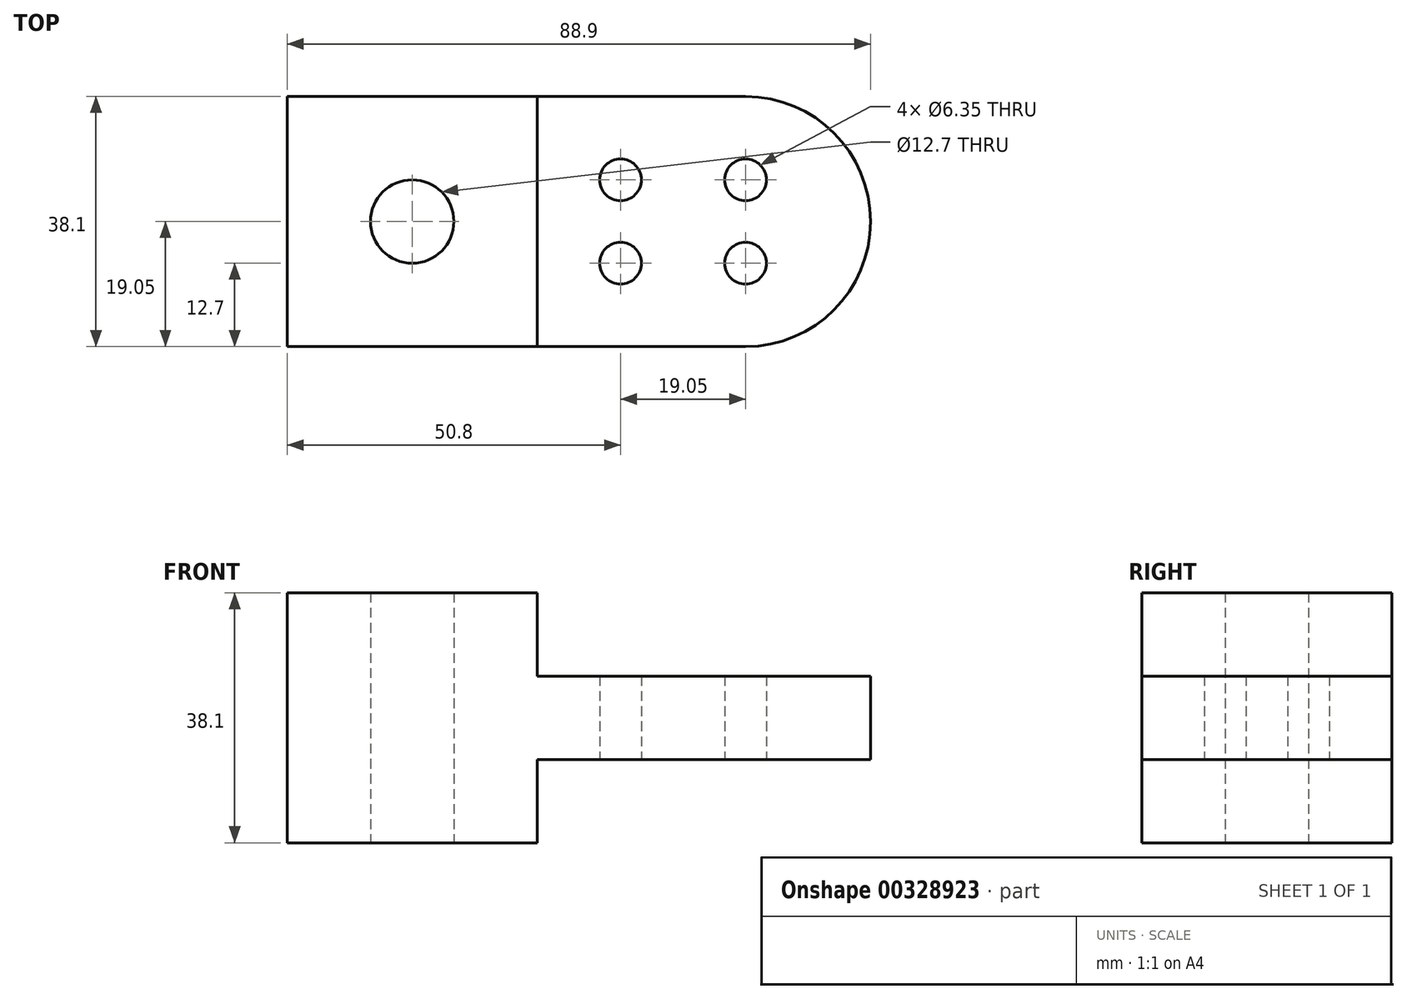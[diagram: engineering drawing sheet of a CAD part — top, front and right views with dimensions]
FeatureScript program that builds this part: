
annotation { "Feature Type Name" : "Feature", "Feature Type Description" : "" }
export const myFeature = defineFeature(function(context is Context, id is Id, definition is map)
    precondition{}
    {
        {
            var Q0;
            Q0=qCreatedBy(makeId("Top.planeOp"),FACE);
            var sketch = newSketch(context, id + "F0", { "sketchPlane" : qUnion([Q0])});
            skLineSegment(sketch, "E0.bottom", {"start": v(0, 0) * mm, "end": v(38.1, 0) * mm});
            skLineSegment(sketch, "E0.top", {"start": v(0, 38.1) * mm, "end": v(38.1, 38.1) * mm});
            skLineSegment(sketch, "E0.left", {"start": v(0, 0) * mm, "end": v(0, 38.1) * mm});
            skLineSegment(sketch, "E0.right", {"start": v(38.1, 0) * mm, "end": v(38.1, 38.1) * mm});
            skLineSegment(sketch, "E1", {"start": v(38.1, 38.1) * mm, "end": v(69.85, 38.1) * mm});
            skLineSegment(sketch, "E2", {"start": v(38.1, 0) * mm, "end": v(69.85, 0) * mm});
            skArc(sketch, "E3", {"start": v(69.85, 38.1) * mm, "mid": v(88.9, 19.05) * mm, "end": v(69.85, 0) * mm});
            skCircle(sketch, "E4", {"center": v(19.05, 19.05) * mm, "radius": 6.35 * mm});
            skCircle(sketch, "E5", {"center": v(50.8, 25.4) * mm, "radius": 3.18 * mm});
            skCircle(sketch, "E6", {"center": v(69.85, 25.4) * mm, "radius": 3.18 * mm});
            skCircle(sketch, "E7", {"center": v(50.8, 12.7) * mm, "radius": 3.18 * mm});
            skCircle(sketch, "E8", {"center": v(69.85, 12.7) * mm, "radius": 3.18 * mm});
            skSolve(sketch);
        }
        {
            var Q0;
            Q0=makeQuery(id+"F0.imprint","IMPRINT",FACE,{"disambiguationData":[TD([[makeQuery(id+"F0.imprint","IMPRINT",EDGE,{"derivedFrom":sQuery(id+"F0.wireOp",EDGE,"E0.bottom")}),1.0]])]});
            extrude(context, id + "F1", {"entities" : qUnion([Q0]), "endBound" : BoundingType.SYMMETRIC, "depth" : 38.1 * mm});
        }
        {
            var Q0;
            Q0=makeQuery(id+"F0.imprint","IMPRINT",FACE,{"disambiguationData":[TD([[makeQuery(id+"F0.imprint","IMPRINT",EDGE,{"derivedFrom":sQuery(id+"F0.wireOp",EDGE,"E0.right")}),-1.0]])]});
            extrude(context, id + "F2", {"entities" : qUnion([Q0]), "operationType" : NewBodyOperationType.ADD, "endBound" : BoundingType.SYMMETRIC, "depth" : 12.7 * mm});
        }
    });
